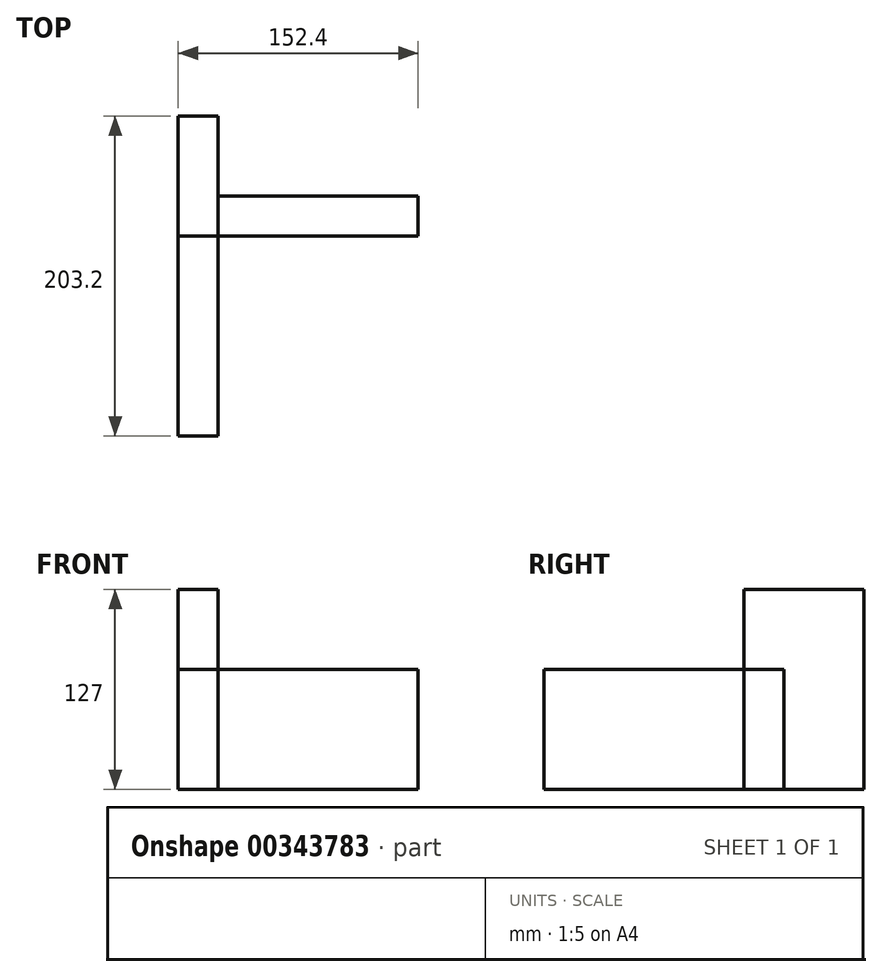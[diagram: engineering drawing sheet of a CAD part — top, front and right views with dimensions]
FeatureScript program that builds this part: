
annotation { "Feature Type Name" : "Feature", "Feature Type Description" : "" }
export const myFeature = defineFeature(function(context is Context, id is Id, definition is map)
    precondition{}
    {
        {
            var Q0;
            Q0=qCreatedBy(makeId("Right.planeOp"),FACE);
            var sketch = newSketch(context, id + "F0", { "sketchPlane" : qUnion([Q0])});
            skLineSegment(sketch, "E0.bottom", {"start": v(0, 0) * mm, "end": v(25.4, 0) * mm});
            skLineSegment(sketch, "E0.top", {"start": v(0, 76.2) * mm, "end": v(25.4, 76.2) * mm});
            skLineSegment(sketch, "E0.left", {"start": v(0, 0) * mm, "end": v(0, 76.2) * mm});
            skLineSegment(sketch, "E0.right", {"start": v(25.4, 0) * mm, "end": v(25.4, 76.2) * mm});
            skSolve(sketch);
        }
        {
            var Q0;
            Q0=makeQuery(id+"F0.imprint","IMPRINT",FACE,{"disambiguationData":[TD([[makeQuery(id+"F0.imprint","IMPRINT",EDGE,{"derivedFrom":sQuery(id+"F0.wireOp",EDGE,"E0.bottom")}),1.0]])]});
            extrude(context, id + "F1", {"entities" : qUnion([Q0]), "depth" : 127 * mm});
        }
        {
            var Q0;
            Q0=qCreatedBy(makeId("Front.planeOp"),FACE);
            var sketch = newSketch(context, id + "F2", { "sketchPlane" : qUnion([Q0])});
            skLineSegment(sketch, "E1.bottom", {"start": v(0, 0) * mm, "end": v(-25.4, 0) * mm});
            skLineSegment(sketch, "E1.top", {"start": v(0, 76.2) * mm, "end": v(-25.4, 76.2) * mm});
            skLineSegment(sketch, "E1.left", {"start": v(0, 0) * mm, "end": v(0, 76.2) * mm});
            skLineSegment(sketch, "E1.right", {"start": v(-25.4, 0) * mm, "end": v(-25.4, 76.2) * mm});
            skSolve(sketch);
        }
        {
            var Q0;
            Q0=makeQuery(id+"F2.imprint","IMPRINT",FACE,{"disambiguationData":[TD([[makeQuery(id+"F2.imprint","IMPRINT",EDGE,{"derivedFrom":sQuery(id+"F2.wireOp",EDGE,"E1.bottom")}),-1.0]])]});
            extrude(context, id + "F3", {"entities" : qUnion([Q0]), "depth" : 127 * mm});
        }
        {
            var Q0;
            Q0=qCreatedBy(makeId("Top.planeOp"),FACE);
            var sketch = newSketch(context, id + "F4", { "sketchPlane" : qUnion([Q0])});
            skLineSegment(sketch, "E2.bottom", {"start": v(0, 0) * mm, "end": v(-25.4, 0) * mm});
            skLineSegment(sketch, "E2.top", {"start": v(0, 76.2) * mm, "end": v(-25.4, 76.2) * mm});
            skLineSegment(sketch, "E2.left", {"start": v(0, 0) * mm, "end": v(0, 76.2) * mm});
            skLineSegment(sketch, "E2.right", {"start": v(-25.4, 0) * mm, "end": v(-25.4, 76.2) * mm});
            skSolve(sketch);
        }
        {
            var Q0;
            Q0=makeQuery(id+"F4.imprint","IMPRINT",FACE,{"disambiguationData":[TD([[makeQuery(id+"F4.imprint","IMPRINT",EDGE,{"derivedFrom":sQuery(id+"F4.wireOp",EDGE,"E2.bottom")}),-1.0]])]});
            extrude(context, id + "F5", {"entities" : qUnion([Q0]), "depth" : 127 * mm});
        }
    });
